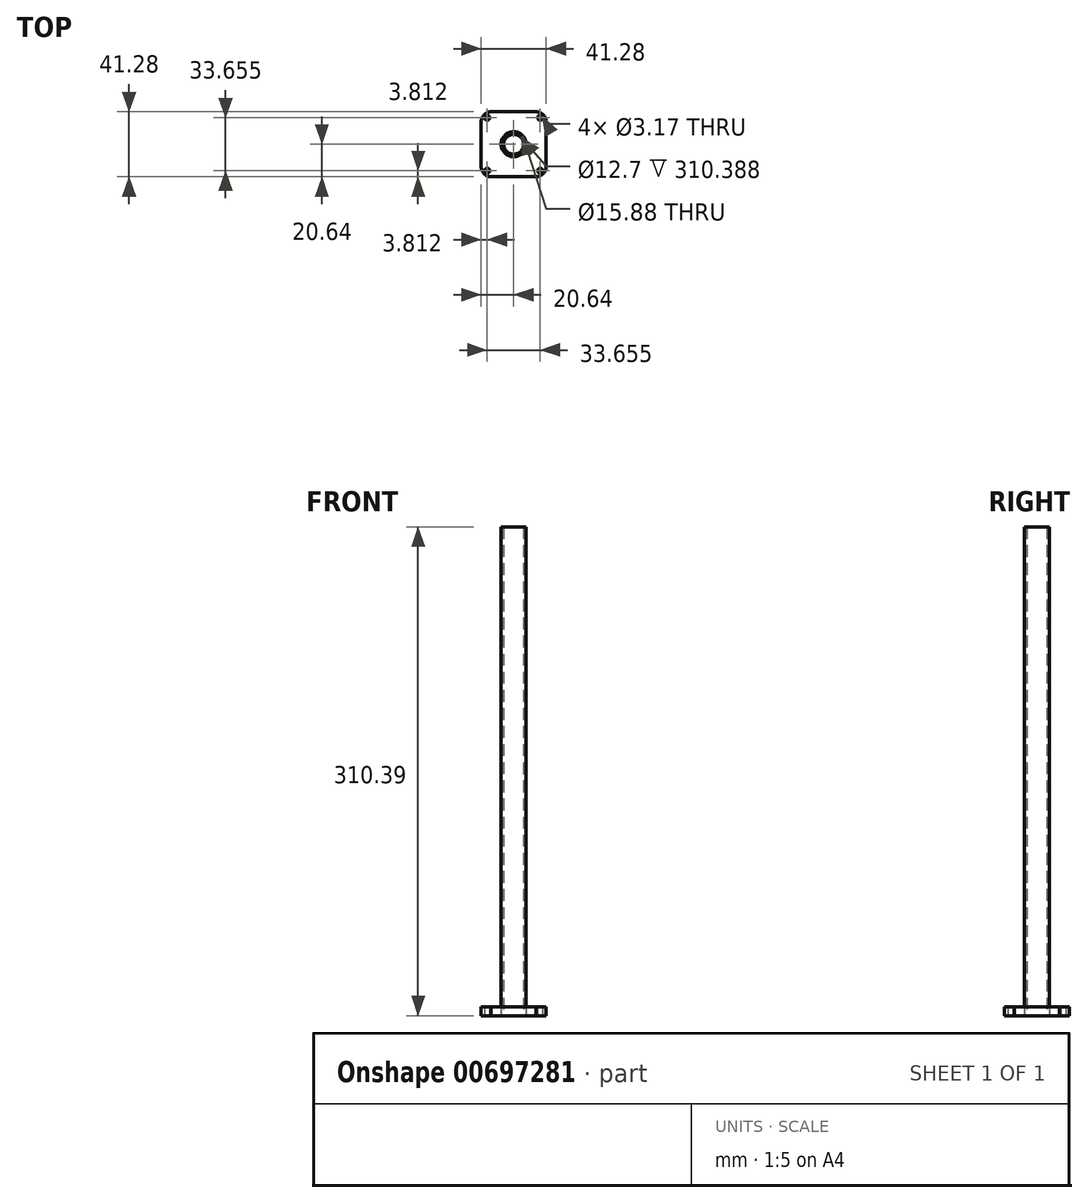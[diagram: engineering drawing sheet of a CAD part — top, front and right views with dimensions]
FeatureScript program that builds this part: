
annotation { "Feature Type Name" : "Feature", "Feature Type Description" : "" }
export const myFeature = defineFeature(function(context is Context, id is Id, definition is map)
    precondition{}
    {
        {
            var Q0;
            Q0=qCreatedBy(makeId("Top.planeOp"),FACE);
            var sketch = newSketch(context, id + "F0", { "sketchPlane" : qUnion([Q0])});
            skCircle(sketch, "E0", {"center": v(0, 0) * mm, "radius": 7.94 * mm});
            skCircle(sketch, "E1", {"center": v(0, 0) * mm, "radius": 6.35 * mm});
            skLineSegment(sketch, "E2.bottom", {"start": v(-20.64, 20.64) * mm, "end": v(20.64, 20.64) * mm});
            skLineSegment(sketch, "E2.top", {"start": v(-20.64, -20.64) * mm, "end": v(20.64, -20.64) * mm});
            skLineSegment(sketch, "E2.left", {"start": v(-20.64, 20.64) * mm, "end": v(-20.64, -20.64) * mm});
            skLineSegment(sketch, "E2.right", {"start": v(20.64, 20.64) * mm, "end": v(20.64, -20.64) * mm});
            skPoint(sketch, "E3", {"position": v(-14.29, 20.64) * mm});
            skPoint(sketch, "E4", {"position": v(-20.64, 14.29) * mm});
            skPoint(sketch, "E5", {"position": v(14.29, 20.64) * mm});
            skPoint(sketch, "E6", {"position": v(20.64, 14.29) * mm});
            skPoint(sketch, "E7", {"position": v(20.64, -14.29) * mm});
            skPoint(sketch, "E8", {"position": v(14.29, -20.64) * mm});
            skPoint(sketch, "E9", {"position": v(-20.64, -14.29) * mm});
            skPoint(sketch, "E10", {"position": v(-14.29, -20.64) * mm});
            skPoint(sketch, "E11", {"position": v(-18.73, 18.73) * mm});
            skPoint(sketch, "E12", {"position": v(-18.73, -18.73) * mm});
            skPoint(sketch, "E13", {"position": v(18.73, -18.73) * mm});
            skPoint(sketch, "E14", {"position": v(18.73, 18.73) * mm});
            skArc(sketch, "E15", {"start": v(-14.29, 20.64) * mm, "mid": v(-18.73, 18.73) * mm, "end": v(-20.64, 14.29) * mm});
            skArc(sketch, "E16", {"start": v(-20.64, -14.29) * mm, "mid": v(-18.73, -18.73) * mm, "end": v(-14.29, -20.64) * mm});
            skArc(sketch, "E17", {"start": v(14.29, -20.64) * mm, "mid": v(18.73, -18.73) * mm, "end": v(20.64, -14.29) * mm});
            skArc(sketch, "E18", {"start": v(20.64, 14.29) * mm, "mid": v(18.73, 18.73) * mm, "end": v(14.29, 20.64) * mm});
            skCircle(sketch, "E19", {"center": v(-16.83, 16.83) * mm, "radius": 1.59 * mm});
            skCircle(sketch, "E20", {"center": v(-16.83, -16.83) * mm, "radius": 1.59 * mm});
            skCircle(sketch, "E21", {"center": v(16.83, -16.83) * mm, "radius": 1.59 * mm});
            skCircle(sketch, "E22", {"center": v(16.83, 16.83) * mm, "radius": 1.59 * mm});
            skSolve(sketch);
        }
        {
            var Q0;
            Q0=makeQuery(id+"F0.imprint","IMPRINT",FACE,{"disambiguationData":[TD([[makeQuery(id+"F0.imprint","IMPRINT",EDGE,{"derivedFrom":sQuery(id+"F0.wireOp",EDGE,"E0")}),-1.0]])]});
            extrude(context, id + "F1", {"entities" : qUnion([Q0]), "depth" : 5.6 * mm, "offsetDistance" : 25.4 * mm});
        }
        {
            var Q0;
            Q0=makeQuery(id+"F0.imprint","IMPRINT",FACE,{"disambiguationData":[TD([[makeQuery(id+"F0.imprint","IMPRINT",EDGE,{"derivedFrom":sQuery(id+"F0.wireOp",EDGE,"E0")}),1.0]])]});
            extrude(context, id + "F2", {"entities" : qUnion([Q0]), "depth" : 310.4 * mm, "offsetDistance" : 25.4 * mm});
        }
    });
